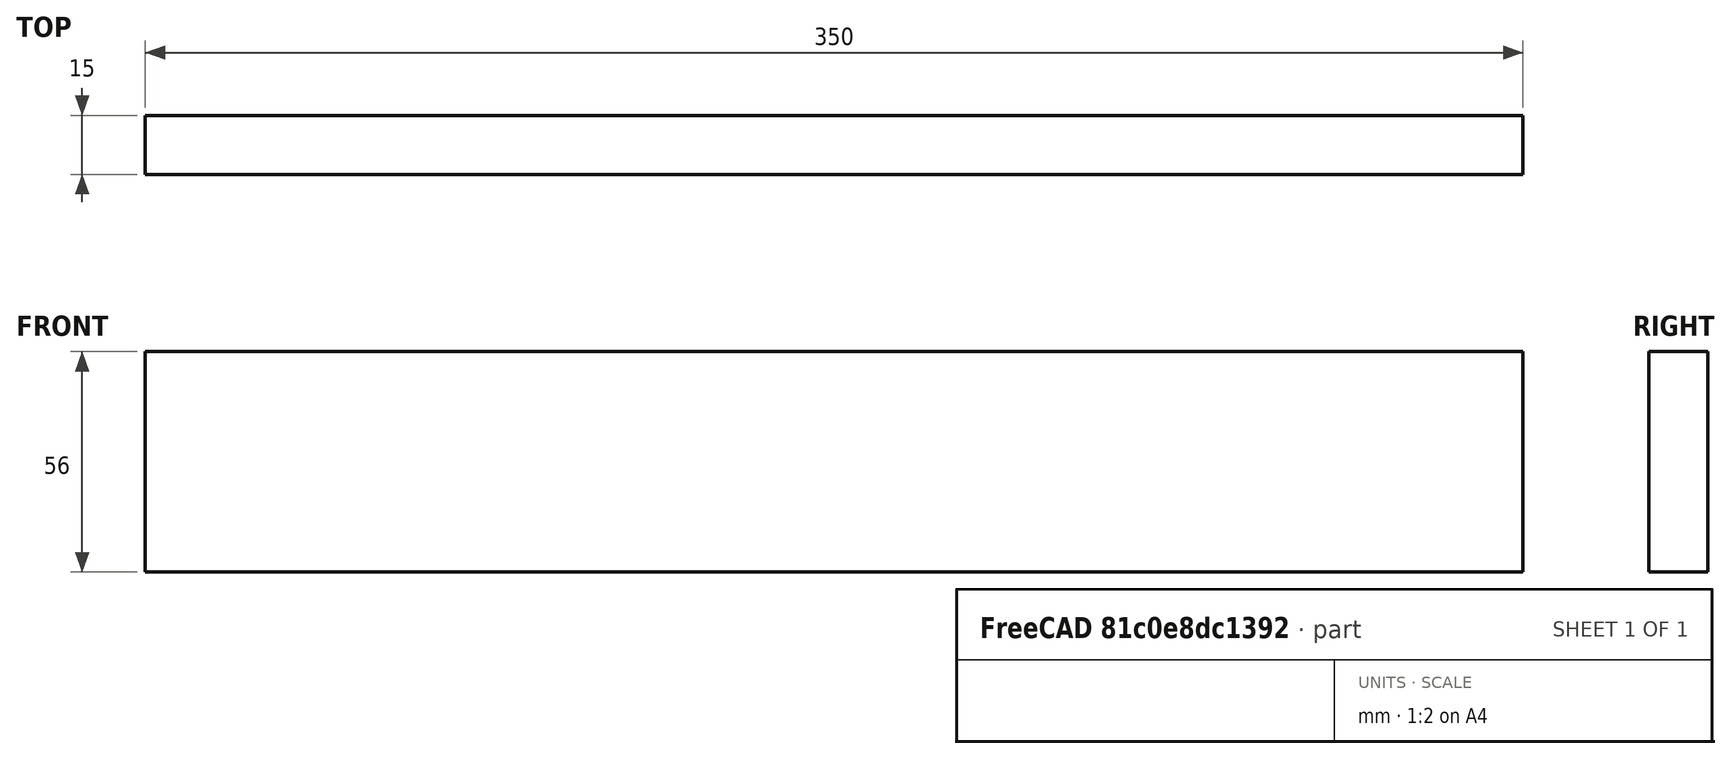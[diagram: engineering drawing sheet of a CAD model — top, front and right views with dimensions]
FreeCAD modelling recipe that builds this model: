
FCSTD DOCUMENT  (FreeCAD 0.18R16110 (Git))
Label: parket
License: All rights reserved
LicenseURL: http://en.wikipedia.org/wiki/All_rights_reserved
objects: Sketcher::SketchObject×1, PartDesign::Pad×1, PartDesign::Body×1
note: 4 computed .brp shape members not serialized (recipe doc carries the construction recipe); baked Part::Feature solids carry a one-line shape summary decoded from their .brp

FEATURE [Sketcher::SketchObject] Sketch
  MapMode = 5
  Support = -> [XY_Plane]
  sketch-geometry (4):
    g0: LineSegment StartX=0 StartY=0 StartZ=0 EndX=350 EndY=0 EndZ=0
    g1: LineSegment StartX=350 StartY=0 StartZ=0 EndX=350 EndY=15 EndZ=0
    g2: LineSegment StartX=350 StartY=15 StartZ=0 EndX=0 EndY=15 EndZ=0
    g3: LineSegment StartX=0 StartY=15 StartZ=0 EndX=0 EndY=0 EndZ=0
  constraints (11):
    c: Coincident(g0,g1)
    c: Coincident(g1,g2)
    c: Coincident(g2,g3)
    c: Coincident(g3,g0)
    c: Horizontal(g0)
    c: Horizontal(g2)
    c: Vertical(g1)
    c: Vertical(g3)
    c: Coincident(g0,g-1)
    c: DistanceX(g0,g0) = 350
    c: DistanceY(g3,g3) = 15
FEATURE [PartDesign::Pad] Pad
  Length = 56
  Length2 = 100
  Profile = -> Sketch
  Type = 0
FEATURE [PartDesign::Body] Body
  Group = -> [Sketch,Pad]
  Origin = -> Origin
  Tip = -> Pad
